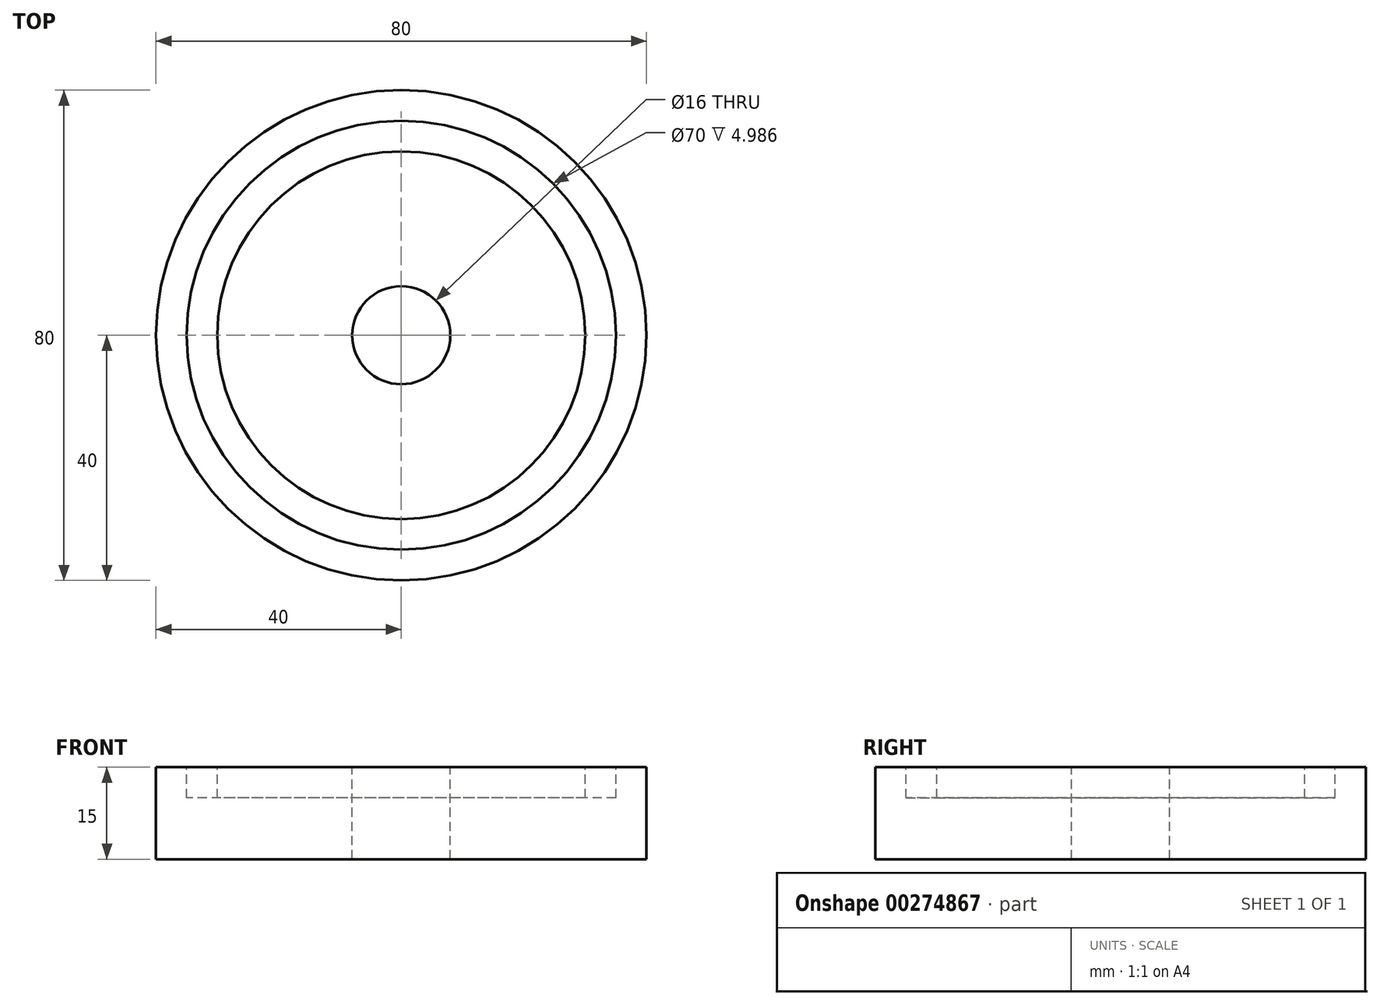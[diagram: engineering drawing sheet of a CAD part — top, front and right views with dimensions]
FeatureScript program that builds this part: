
annotation { "Feature Type Name" : "Feature", "Feature Type Description" : "" }
export const myFeature = defineFeature(function(context is Context, id is Id, definition is map)
    precondition{}
    {
        {
            var Q0;
            Q0=qCreatedBy(makeId("Front.planeOp"),FACE);
            var sketch = newSketch(context, id + "F0", { "sketchPlane" : qUnion([Q0])});
            skLineSegment(sketch, "E0", {"start": v(-40, 15) * mm, "end": v(-40, 0) * mm});
            skLineSegment(sketch, "E1", {"start": v(-40, 0) * mm, "end": v(-8, 0) * mm});
            skLineSegment(sketch, "E2", {"start": v(-8, 0) * mm, "end": v(-8, 15) * mm});
            skLineSegment(sketch, "E3", {"start": v(-8, 15) * mm, "end": v(-30, 15) * mm});
            skLineSegment(sketch, "E4", {"start": v(-30, 15) * mm, "end": v(-30, 10) * mm});
            skLineSegment(sketch, "E5", {"start": v(-30, 10) * mm, "end": v(-35, 10) * mm});
            skLineSegment(sketch, "E6", {"start": v(-35, 10) * mm, "end": v(-35, 14.99) * mm});
            skLineSegment(sketch, "E7", {"start": v(-35, 14.99) * mm, "end": v(-40, 15) * mm});
            skLineSegment(sketch, "E8", {"start": v(0, 19.04) * mm, "end": v(0, 0) * mm, "construction": true});
            skSolve(sketch);
        }
        {
            var Q0;
            Q0=makeQuery(id+"F0.imprint","IMPRINT",FACE,{"disambiguationData":[TD([[makeQuery(id+"F0.imprint","IMPRINT",EDGE,{"derivedFrom":sQuery(id+"F0.wireOp",EDGE,"E0")}),1.0]])]});
            var Q1;
            Q1=sQuery(id+"F0.wireOp",EDGE,"E8");
            revolve(context, id + "F1", {"entities" : qUnion([Q0]), "axis" : qUnion([Q1]), "revolveType" : RevolveType.FULL});
        }
    });
